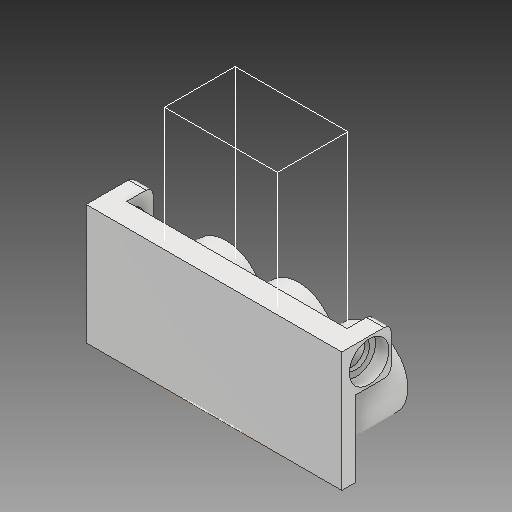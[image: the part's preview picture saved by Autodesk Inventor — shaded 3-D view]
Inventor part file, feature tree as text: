
AUTODESK INVENTOR PART (.ipt)
format: ipt  version: 2018 (Build 220112000, 112)  size: 1,073,664 bytes
history: native  units: mm
features: sketch x60, extrude x49, fillet x5
ambient origin geometry x8: Origin, YZ Plane, XZ Plane, XY Plane, X Axis, Y Axis, Z Axis, Center Point
bodies: Solid1 (feature_tree)
feature tree (114):
  extrude  "Extrusion1"  Depth=80.0mm
  extrude  "Extrusion2"  Depth=3.0mm
  sketch  "Sketch3"  dims[d5=12.0mm d6=14.5mm]
  extrude  "Extrusion3"  Depth=14.5mm
  extrude  "Extrusion4"  Depth=2.0mm
  extrude  "Extrusion5"  Depth=0.5mm TaperAngle=0.0deg
  sketch  "Sketch7"  dims[d15=10.0mm d16=25.0mm]
  extrude  "Extrusion6"  Depth=25.0mm
  extrude  "Extrusion7"  Depth=25.0mm
  extrude  "Extrusion8"  Depth=10.0mm
  fillet  "Fillet1"  Radius=10.0mm
  fillet  "Fillet2"  Radius=10.0mm
  extrude  "Extrusion9"  Depth=2.5mm TaperAngle=0.0deg
  extrude  "Extrusion10"  Depth=4.0mm
  fillet  "Fillet3"  Radius=3.0mm
  extrude  "Extrusion11"  Depth=21.0mm
  extrude  "Extrusion12"  Depth=41.0mm
  extrude  "Extrusion13"  Depth=42.0mm
  extrude  "Extrusion14"  Depth=38.0mm
  extrude  "Extrusion15"  Depth=45.0mm TaperAngle=0.0deg
  extrude  "Extrusion16"  Depth=3.0mm TaperAngle=0.0deg
  extrude  "Extrusion17"  Depth=3.0mm
  extrude  "Extrusion18"  Depth=39.5mm
  extrude  "Extrusion19"  Depth=7.25mm
  extrude  "Extrusion20"  Depth=7.75mm
  extrude  "Extrusion21"  Depth=10.0mm
  sketch  "Sketch24"  dims[d65=66.0mm d66=3.5mm d67=0.0mm]
  extrude  "Extrusion22"  Depth=10.0mm TaperAngle=0.0deg
  extrude  "Extrusion23"  Depth=16.0mm
  extrude  "Extrusion24"  Depth=3.5mm TaperAngle=0.0deg
  extrude  "Extrusion25"  Depth=2.0mm
  extrude  "Extrusion26"  Depth=2.0mm TaperAngle=0.0deg
  sketch  "Sketch30"  dims[d81=4.0mm d82=4.0mm]
  extrude  "Extrusion27"  Depth=16.0mm
  extrude  "Extrusion28"  Depth=2.0mm
  extrude  "Extrusion29"  Depth=3.5mm TaperAngle=0.0deg
  sketch  "Sketch34"  dims[d91=5.0mm d92=16.0mm d93=5.0mm]
  extrude  "Extrusion30"  Depth=4.0mm
  extrude  "Extrusion31"  Depth=2.0mm TaperAngle=0.0deg
  extrude  "Extrusion32"  Depth=150.0mm TaperAngle=0.0deg
  sketch  "Sketch38"  dims[d102=5.0mm d103=0.0mm d104=500.0mm d105=0.0mm]
  extrude  "Extrusion33"  Depth=16.0mm
  sketch  "Sketch40"  dims[d110=38.75mm d111=38.75mm]
  extrude  "Extrusion34"  Depth=16.0mm
  fillet  "Fillet4"  Radius=5.0mm
  extrude  "Extrusion35"  Depth=3.0mm
  extrude  "Extrusion36"  Depth=43.0mm TaperAngle=0.0deg
  extrude  "Extrusion37"  Depth=38.75mm
  extrude  "Extrusion38"  Depth=5.0mm TaperAngle=0.0deg
  extrude  "Extrusion39"  Depth=45.0mm TaperAngle=0.0deg
  extrude  "Extrusion40"  Depth=38.75mm
  sketch  "Sketch48"  dims[d134=16.0mm d135=5.0mm d136=0.0mm d137=7.0mm]
  extrude  "Extrusion41"  Depth=3.5mm TaperAngle=0.0deg
  extrude  "Extrusion42"  Depth=100.0mm TaperAngle=0.0deg
  extrude  "Extrusion43"  Depth=1.5mm TaperAngle=0.0deg
  sketch  "Sketch52"  dims[d144=16.0mm]
  extrude  "Extrusion44"  Depth=10.0mm
  extrude  "Extrusion45"  Depth=10.0mm
  extrude  "Extrusion46"  Depth=7.0mm
  sketch  "Sketch56"  dims[d150=5.0mm d151=0.0mm]
  sketch  "Sketch57"  dims[d152=5.0mm d153=0.0mm]
  extrude  "Extrusion47"  Depth=7.75mm
  extrude  "Extrusion48"  Depth=5.0mm TaperAngle=0.0deg
  fillet  "Fillet5"  Radius=7.0mm
  extrude  "Extrusion49"  Depth=15.0mm TaperAngle=0.0deg
  sketch  "Sketch1"  dims[d0=145.0mm d1=80.0mm]
  sketch  "Sketch2"  dims[d2=3.0mm d3=0.0mm d4=12.0mm]
  sketch  "Sketch4"  dims[d7=2.0mm d8=2.0mm]
  sketch  "Sketch5"  dims[d9=6.0mm d10=0.0mm d11=0.5mm d12=0.0mm]
  sketch  "Sketch6"  dims[d13=10.0mm d14=25.0mm]
  sketch  "Sketch8"  dims[d17=25.0mm d18=0.0mm d19=22.5mm d20=10.0mm d21=0.0mm d22=10.0mm]
  sketch  "Sketch9"  dims[d23=2.5mm d24=0.0mm d25=7.5mm d26=0.0mm]
  sketch  "Sketch10"  dims[d27=10.0mm d28=0.0mm d29=4.0mm d30=3.0mm]
  sketch  "Sketch11"  dims[d31=1.0mm d32=21.0mm]
  sketch  "Sketch12"  dims[d33=38.0mm d34=41.0mm]
  sketch  "Sketch13"  dims[d35=38.0mm d36=42.0mm]
  sketch  "Sketch14"  dims[d37=41.0mm d38=38.0mm]
  sketch  "Sketch15"  dims[d39=42.0mm d40=45.0mm d41=0.0mm]
  sketch  "Sketch16"  dims[d42=12.5mm d43=3.0mm d44=0.0mm]
  sketch  "Sketch17"  dims[d45=3.0mm d46=39.5mm]
  sketch  "Sketch18"  dims[d47=39.5mm d48=39.5mm]
  sketch  "Sketch19"  dims[d49=45.0mm d50=0.0mm d51=7.25mm]
  sketch  "Sketch20"  dims[d52=4.0mm d53=7.75mm d54=0.0mm d55=0.0mm d56=125.0mm]
  sketch  "Sketch21"  dims[d57=10.0mm d58=0.0mm d59=1.0mm]
  sketch  "Sketch22"  dims[d60=14.5mm d61=10.0mm d62=0.0mm]
  sketch  "Sketch23"  dims[d63=16.0mm d64=12.0mm]
  sketch  "Sketch25"  dims[d68=4.0mm d69=2.0mm]
  sketch  "Sketch26"  dims[d70=4.0mm d71=2.0mm d72=0.0mm]
  sketch  "Sketch27"  dims[d73=2.0mm d74=0.0mm d75=16.0mm]
  sketch  "Sketch28"  dims[d76=2.0mm d77=2.0mm]
  sketch  "Sketch29"  dims[d78=2.0mm d79=3.5mm d80=0.0mm]
  sketch  "Sketch31"  dims[d83=4.0mm d84=2.0mm d85=0.0mm]
  sketch  "Sketch32"  dims[d86=15.5mm d87=150.0mm d88=0.0mm]
  sketch  "Sketch33"  dims[d89=12.0mm d90=16.0mm]
  sketch  "Sketch35"  dims[d94=12.0mm d95=3.0mm]
  sketch  "Sketch36"  dims[d96=43.0mm d97=0.0mm d98=43.0mm d99=0.0mm]
  sketch  "Sketch37"  dims[d100=38.75mm d101=38.75mm]
  sketch  "Sketch39"  dims[d106=45.0mm d107=0.0mm d108=45.0mm d109=0.0mm]
  sketch  "Sketch41"  dims[d112=45.0mm d113=0.0mm d114=3.5mm d115=0.0mm]
  sketch  "Sketch42"  dims[d116=43.0mm d117=0.0mm d118=100.0mm d119=0.0mm]
  sketch  "Sketch43"  dims[d120=200.0mm d121=0.0mm d122=1.5mm d123=0.0mm]
  sketch  "Sketch44"  dims[d124=5.0mm d125=10.0mm]
  sketch  "Sketch45"  dims[d126=10.0mm d127=6.35mm]
  sketch  "Sketch46"  dims[d128=7.0mm d129=0.0mm d130=2.75mm]
  sketch  "Sketch47"  dims[d131=7.0mm d132=0.0mm d133=7.75mm]
  sketch  "Sketch49"  dims[d138=7.0mm d139=15.0mm d140=0.0mm]
  sketch  "Sketch50"  dims[d141=13.5mm]
  sketch  "Sketch51"  dims[d142=2.0mm d143=0.0mm]
  sketch  "Sketch53"  dims[d145=5.0mm d146=0.0mm]
  sketch  "Sketch54"  dims[d147=2.0mm d148=0.0mm]
  sketch  "Sketch55"  dims[d149=16.25mm]
  sketch  "Sketch58"  dims[d154=3.0mm d155=0.0mm]
  sketch  "Sketch59"  dims[d156=3.0mm d157=0.0mm]
  sketch  "Sketch60"  dims[d158=12.25mm d159=3.5mm d160=43.0mm d161=0.0mm d162=12.25mm d163=3.5mm d164=43.0mm d165=0.0mm d166=18.0mm d167=43.0mm d168=0.0mm d169=131.0mm d170=0.0mm d171=131.0mm d172=0.0mm d173=0.5mm d174=2.0mm d175=0.0mm]
